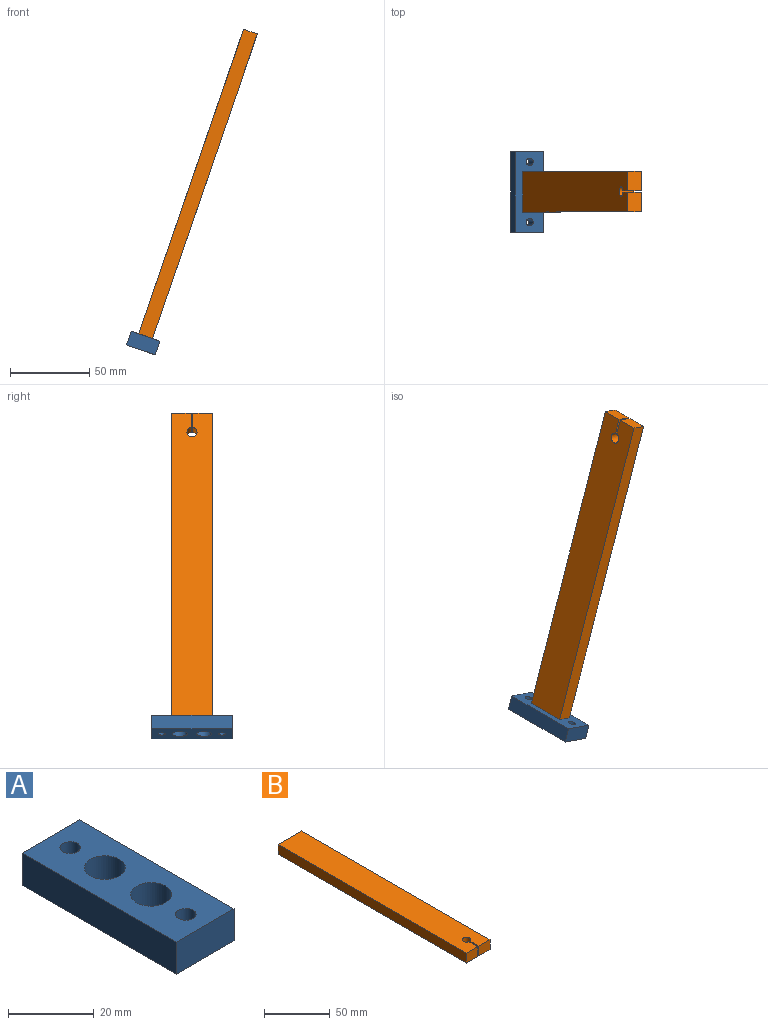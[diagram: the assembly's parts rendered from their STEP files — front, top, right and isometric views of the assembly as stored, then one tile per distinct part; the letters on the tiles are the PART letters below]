
ASSEMBLY  parts=2 mates=1
PART A: 14 faces, bbox 19.1x50.8x9.1 mm
  f0: cylinder r=2.38mm len=4.76mm, axis (0,0,1), area 32.3mm2, adj f7,f10
  f1: cylinder r=2.38mm len=4.76mm, axis (0,0,1), area 32.3mm2, adj f7,f8
  f2: plane 50.8x9.14mm, normal (1,0,0), area 464.5mm2, adj f3,f5,f6,f7
  f3: plane 19.05x9.14mm, normal (0,1,0), area 174.2mm2, adj f2,f4,f6,f7
  f4: plane 50.8x9.14mm, normal (-1,0,0), area 464.5mm2, adj f3,f5,f6,f7
  f5: plane 19.05x9.14mm, normal (0,-1,0), area 174.2mm2, adj f2,f4,f6,f7
  f6: plane 50.8x19.05mm, normal (0,0,1), area 789.6mm2, adj f2,f3,f4,f5,f9,f11,f12,f13
  f7: plane 50.8x19.05mm, normal (0,0,-1), area 896.5mm2, adj f0,f1,f2,f3,f4,f5,f12,f13
  f8: plane 9.53x9.53mm, normal (0,0,1), area 53.4mm2, adj f1,f9
  f9: cylinder r=4.76mm len=9.53mm, axis (0,0,1), area 209mm2, adj f6,f8
  f10: plane 9.53x9.53mm, normal (0,0,1), area 53.4mm2, adj f0,f11
  f11: cylinder r=4.76mm len=9.53mm, axis (0,0,1), area 209mm2, adj f6,f10
  f12: cylinder r=2.38mm len=9.14mm, axis (0,0,1), area 136.8mm2, adj f6,f7
  f13: cylinder r=2.38mm len=9.14mm, axis (0,0,1), area 136.8mm2, adj f6,f7
PART B: 14 faces, bbox 25.4x203.2x9.1 mm
  f0: plane 12.1x9.14mm, normal (0,-1,0), area 110.7mm2, adj f4,f5,f6,f9
  f1: plane 12.1x9.14mm, normal (0,-1,0), area 110.7mm2, adj f2,f5,f6,f7
  f2: plane 203.2x9.14mm, normal (1,0,0), area 1858.1mm2, adj f1,f3,f5,f6
  f3: plane 25.4x9.14mm, normal (0,1,0), area 196.6mm2, adj f2,f4,f5,f6,f10,f12
  f4: plane 203.2x9.14mm, normal (-1,0,0), area 1858.1mm2, adj f0,f3,f5,f6
  f5: plane 203.2x25.4mm, normal (0,0,1), area 5118.2mm2, adj f0,f1,f2,f3,f4,f7,f8,f9
  f6: plane 203.2x25.4mm, normal (0,0,-1), area 5118.2mm2, adj f0,f1,f2,f3,f4,f7,f8,f9
  f7: plane 9.58x9.14mm, normal (-1,0,0), area 87.6mm2, adj f1,f5,f6,f8
  f8: cylinder r=3.17mm len=9.14mm, axis (0,0,1), area 171.5mm2, adj f5,f6,f7,f9
  f9: plane 9.58x9.14mm, normal (1,0,0), area 87.6mm2, adj f0,f5,f6,f8
  f10: cylinder r=2.38mm len=12.7mm, axis (0,1,0), area 190mm2, adj f3,f11
  f11: plane 4.76x4.76mm, normal (0,1,0), area 17.8mm2, adj f10
  f12: cylinder r=2.38mm len=12.7mm, axis (0,1,0), area 190mm2, adj f3,f13
  f13: plane 4.76x4.76mm, normal (0,1,0), area 17.8mm2, adj f12
PLACE A rot(axis=(0,-1,0),161deg) t=(12.66,13.85,-37.65)mm
PLACE B rot(axis=(-0.63,0.63,-0.45),131.5deg) t=(41.41,13.85,59.9)mm
MATE fastened A.f0 <-> B.f12  axis (0.33,0,0.95) through (12.66,6.23,-37.65)mm
